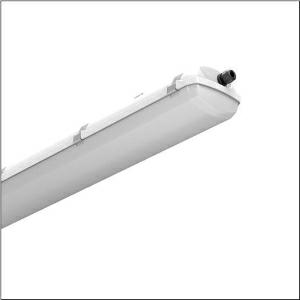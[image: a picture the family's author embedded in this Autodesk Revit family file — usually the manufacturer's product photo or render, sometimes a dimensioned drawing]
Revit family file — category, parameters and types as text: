
# Revit family: monsun_r__ex_51fxa27l840a_cf3b
name_source: partatom
category: Lighting Fixtures
units: mm (PartAtom-declared; Revit-internal decimal feet)

## family parameters
Cut with Voids When Loaded = No
Host = Face
Light Source = No
Part Type = Normal
Room Calculation Point = No
Round Connector Dimension = Use Diameter
Shared = No

## types (1)
- Monsun® Ex (1 x LED, 4650 lm, 33 W, 6500K)
    Apparent Load = 33 VA
    CIE Flux Codes = 46 76 94 98 100
    Color Rendering = 80
    Color Temperature = 6500K
    Default Elevation = 1800 mm
    Description = Monsun® Ex, damp-proof luminaire, primary optical cover: cover, of PC, UV-stabilised, opal, light emission: direct distribution, primary light characteristic: symmetric, installation type: surface-mounted, LED, rated luminous flux: 4.650lm, luminous efficacy: 141lm/W, light colour: 860, colour temperature: 6000K, control gear: ON/OFF, with terminal, 3-pole, max. 2.5mm², through-wiring: 5x 2.5mm², mains connection: 220..250V, AC, 50/60Hz, rated input power: 33W, housing, of PC, light grey (RAL 7035), incl. 1x Ex cable gland M20 for cable diameter 7..12mm with sealing, incl. 1x Ex locking screw M20 with sealing, length: 1.280mm, width: 155mm, height: 105mm, clip for enclosure, of stainless steel, protection rating (complete): IP66, insulation class (complete): insulation class I (protective earthing), certification: CE, explosion class: zone 1,21 II 2G Ex eb mb op is IIC T4 Gb, II 2D Ex tb op is IIIC T67°C Db, impact resistance: IK10, permissible operating ambient temperature: -20..+40°C, contact your sales advisor before using the luminaires in applications with unclear chemical exposure, large temperature fluctuations or condensation-forming humidity, packaging unit: 1 piece
    Height = 105 mm
    Lamp = 1 x LED
    Lamp Light Flux = 4650 lm
    Lamp Power = 33 W
    Lamp count = 1
    Length = 1280 mm
    Luminous efficacy = 141 lm/W
    Manufacturer = Siteco
    ModVariant = No
    Model = 51FXA27L840A
    Mounting Place = Ceiling
    Mounting Type = Surface mounted
    Number of Poles = 1
    OnlyDefault = Yes
    Power Factor = 1
    Product Name = Monsun® Ex
    Product group = damp-proof luminaire
    ProductGroupID = 300
    Protection Class = Protection class I
    Protection Degree = IP 66
    RLX_Detail_Level = 1
    RLX_Emergency_Light_Flux = 0 lm
    RLX_Emergency_Type = 0
    RLX_Emergency_Type_DB = No
    RlxData = <blob elided: 41685 chars, md5=db916c41>
    Socket = socket
    Standby Power = 0 W
    System Light Flux = 4650 lm
    System Power = 33 W
    Type Comments = Product without accessories
    Type Image = l_1258882.jpg
    URL = http://relux.com
    VarID = ---
    Voltage = 0 V
    Weight = 0.00 kg
    Width = 155 mm

## geometry (parser evidence)
native form markers: Blend x4, Sweep x7
no freeform markers — native parametric forms only
